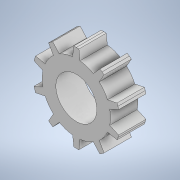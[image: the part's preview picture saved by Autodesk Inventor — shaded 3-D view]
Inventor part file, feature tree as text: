
AUTODESK INVENTOR PART (.ipt)
format: ipt  version: 2021 (Build 250183000, 183)  size: 173,568 bytes
history: native  units: in
note: dims shown in document units (in); Inventor stores cm internally (conversion verified against a paired STEP export)
features: extrude x1, sketch x1
ambient origin geometry x8: Origin, YZ Plane, XZ Plane, XY Plane, X Axis, Y Axis, Z Axis, Center Point
bodies: Solid1 (feature_tree)
feature tree (2):
  extrude  "Extrusion1"  [1 undecoded]
  sketch  "Sketch1"  dims[d0=0.7874in d1=0.0in]
note: 1 required parameter value undecoded (feature->parameter linkage not recoverable at this tier; creation-order binding heuristic only, values carry confidence <= 0.55)
